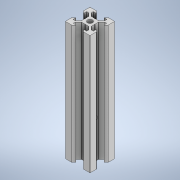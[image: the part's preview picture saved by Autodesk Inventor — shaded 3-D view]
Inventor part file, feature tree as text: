
AUTODESK INVENTOR PART (.ipt)
format: ipt  version: 2021 (Build 250183000, 183)  size: 324,096 bytes
history: native  units: mm
features: sketch x5, hole x3, extrude x2, fillet x2, other x1, pattern_circular x1, projected_geometry x1
ambient origin geometry x8: Origin, YZ Plane, XZ Plane, XY Plane, X Axis, Y Axis, Z Axis, Center Point
bodies: Body1 (feature_tree)
feature tree (15):
  other  "實體1"
  extrude  "擠出1"  Depth=20.0mm
  extrude  "擠出2"  Depth=20.0mm
  fillet  "圓角1"  Radius=96.5mm
  pattern_circular  "環形陣列1"  [2 undecoded]
  hole  "孔1"  [1 undecoded]
  fillet  "圓角2"  Radius=6.2mm
  hole  "孔2"  [1 undecoded]
  hole  "孔3"  [1 undecoded]
  sketch  "草圖1"
  sketch  "草圖2"
  projected_geometry  "投影迴路1"
  sketch  "草圖3"
  sketch  "草圖4"
  sketch  "草圖5"
note: 5 required parameter values undecoded (feature->parameter linkage not recoverable at this tier; creation-order binding heuristic only, values carry confidence <= 0.55)
